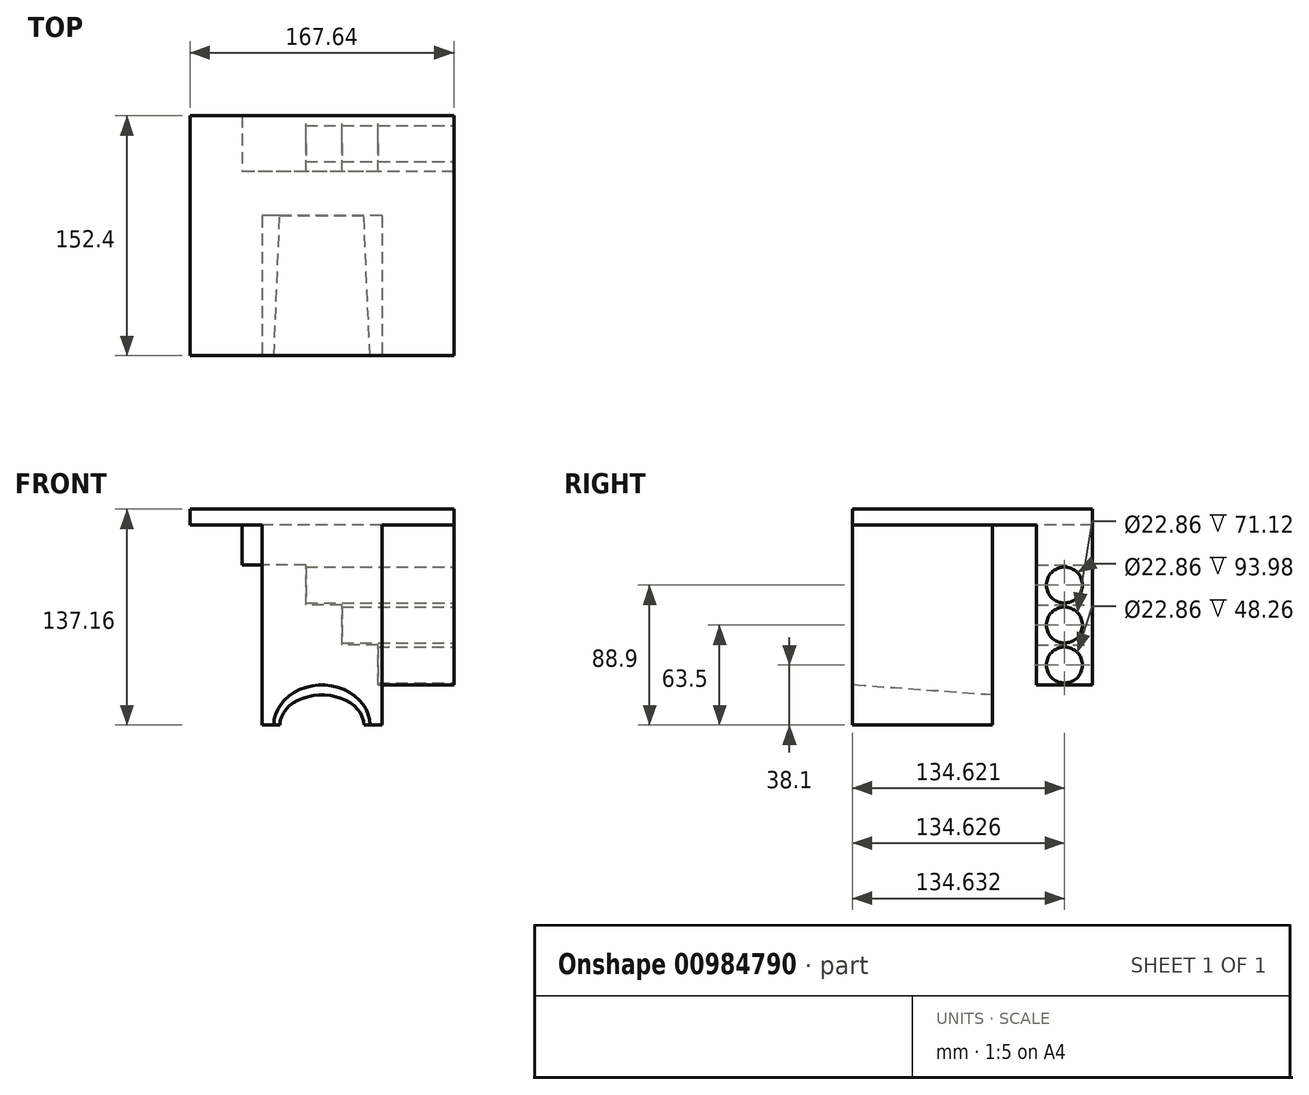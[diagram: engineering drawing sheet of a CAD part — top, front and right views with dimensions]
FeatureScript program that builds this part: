
annotation { "Feature Type Name" : "Feature", "Feature Type Description" : "" }
export const myFeature = defineFeature(function(context is Context, id is Id, definition is map)
    precondition{}
    {
        {
            var Q0;
            Q0=qCreatedBy(makeId("Top.planeOp"),FACE);
            var sketch = newSketch(context, id + "F0", { "sketchPlane" : qUnion([Q0])});
            skLineSegment(sketch, "E0.bottom", {"start": v(-69.25, 110.43) * mm, "end": v(32.35, 110.43) * mm});
            skLineSegment(sketch, "E0.top", {"start": v(-69.25, -41.97) * mm, "end": v(32.35, -41.97) * mm});
            skLineSegment(sketch, "E0.left", {"start": v(-69.25, 110.43) * mm, "end": v(-69.25, -41.97) * mm});
            skLineSegment(sketch, "E0.right", {"start": v(32.35, 110.43) * mm, "end": v(32.35, -41.97) * mm});
            skLineSegment(sketch, "E1", {"start": v(32.35, 110.43) * mm, "end": v(65.37, 110.43) * mm});
            skLineSegment(sketch, "E2", {"start": v(65.37, 110.43) * mm, "end": v(65.37, -41.97) * mm});
            skLineSegment(sketch, "E3", {"start": v(65.37, -41.97) * mm, "end": v(32.35, -41.97) * mm});
            skLineSegment(sketch, "E4.bottom", {"start": v(-69.25, 110.43) * mm, "end": v(-102.27, 110.43) * mm});
            skLineSegment(sketch, "E4.top", {"start": v(-69.25, -41.97) * mm, "end": v(-102.27, -41.97) * mm});
            skLineSegment(sketch, "E4.right", {"start": v(-102.27, 110.43) * mm, "end": v(-102.27, -41.97) * mm});
            skSolve(sketch);
        }
        {
            var Q0;
            Q0=makeQuery(id+"F0.imprint","IMPRINT",FACE,{"disambiguationData":[TD([[makeQuery(id+"F0.imprint","IMPRINT",EDGE,{"derivedFrom":sQuery(id+"F0.wireOp",EDGE,"E0.bottom")}),-1.0]])]});
            extrude(context, id + "F1", {"entities" : qUnion([Q0]), "depth" : 10.16 * mm, "offsetDistance" : 25.4 * mm});
        }
        {
            var Q0;
            Q0=makeQuery(id+"F1.opExtrude","CAP_FACE",FACE,{"disambiguationData":[OSD([sQuery(id+"F0.wireOp",EDGE,"E0.bottom"),sQuery(id+"F0.wireOp",EDGE,"E0.top"),sQuery(id+"F0.wireOp",EDGE,"E0.left"),sQuery(id+"F0.wireOp",EDGE,"E0.right")])],"isStart":true});
            var sketch = newSketch(context, id + "F2", { "sketchPlane" : qUnion([Q0])});
            skLineSegment(sketch, "E5", {"start": v(-18.45, -110.43) * mm, "end": v(-18.45, 53.26) * mm, "construction": true});
            skPoint(sketch, "E5.endSnap0", {"position": v(-18.45, 41.97) * mm});
            skLineSegment(sketch, "E6", {"start": v(32.35, -34.23) * mm, "end": v(-139.29, -34.23) * mm, "construction": true});
            skLineSegment(sketch, "E7.bottom", {"start": v(19.65, -46.93) * mm, "end": v(-56.55, -46.93) * mm});
            skLineSegment(sketch, "E7.top", {"start": v(19.65, 41.97) * mm, "end": v(-56.55, 41.97) * mm});
            skLineSegment(sketch, "E7.left", {"start": v(19.65, -46.93) * mm, "end": v(19.65, 41.97) * mm});
            skLineSegment(sketch, "E7.right", {"start": v(-56.55, -46.93) * mm, "end": v(-56.55, 41.97) * mm});
            skSolve(sketch);
        }
        {
            var Q0;
            Q0=makeQuery(id+"F2.imprint","IMPRINT",FACE,{"disambiguationData":[TD([[makeQuery(id+"F2.imprint","IMPRINT",EDGE,{"derivedFrom":sQuery(id+"F2.wireOp",EDGE,"E7.bottom")}),-1.0]])]});
            extrude(context, id + "F3", {"entities" : qUnion([Q0]), "operationType" : NewBodyOperationType.ADD, "depth" : 127 * mm, "offsetDistance" : 25.4 * mm});
        }
        {
            var Q0;
            Q0=makeQuery(id+"F3.boolean.opBoolean","MERGE",FACE,{"derivedFrom":[makeQuery(id+"F1.opExtrude","SWEPT_FACE",FACE,{"disambiguationData":[OSD([sQuery(id+"F0.wireOp",EDGE,"E0.top")])]}),makeQuery(id+"F3.opExtrude","SWEPT_FACE",FACE,{"disambiguationData":[OSD([sQuery(id+"F2.wireOp",EDGE,"E7.top")])]})]});
            var sketch = newSketch(context, id + "F4", { "sketchPlane" : qUnion([Q0])});
            skEllipse(sketch, "E8", {"center": v(-18.45, -127) * mm, "majorRadius": 30.48 * mm, "minorRadius": 25.4 * mm, "majorAxis": v(-1, 0)});
            skSolve(sketch);
        }
        {
            var Q0;
            Q0=makeQuery(id+"F3.opExtrude","SWEPT_FACE",FACE,{"disambiguationData":[OSD([sQuery(id+"F2.wireOp",EDGE,"E7.bottom")])]});
            var sketch = newSketch(context, id + "F5", { "sketchPlane" : qUnion([Q0])});
            skEllipse(sketch, "E9", {"center": v(18.45, -127) * mm, "majorRadius": 26.67 * mm, "minorRadius": 19.05 * mm, "majorAxis": v(-1, 0)});
            skSolve(sketch);
        }
        {
            var Q1;
            {var subQ0=sQuery(id+"F4.wireOp",EDGE,"E8");var subQ1=makeQuery(id+"F3.opExtrude","CAP_EDGE",EDGE,{"disambiguationData":[OSD([sQuery(id+"F2.wireOp",EDGE,"E7.top")])],"isStart":false});var subQ2=makeQuery(id+"F4.imprint","INTERSECT",VERTEX,{"disambiguationData":[OD(0.0)],"derivedFrom":[subQ1,subQ0]});Q1=makeQuery(id+"F4.imprint","IMPRINT",FACE,{"disambiguationData":[TD([[makeQuery(id+"F4.imprint","IMPRINT",EDGE,{"disambiguationData":[TD([[subQ2,1.0]])],"derivedFrom":subQ0}),1.0]])]});}
            var Q2;
            {var subQ0=sQuery(id+"F5.wireOp",EDGE,"E9");var subQ1=makeQuery(id+"F3.opExtrude","CAP_EDGE",EDGE,{"disambiguationData":[OSD([sQuery(id+"F2.wireOp",EDGE,"E7.bottom")])],"isStart":false});var subQ2=makeQuery(id+"F5.imprint","INTERSECT",VERTEX,{"disambiguationData":[OD(0.0)],"derivedFrom":[subQ1,subQ0]});Q2=makeQuery(id+"F5.imprint","IMPRINT",FACE,{"disambiguationData":[TD([[makeQuery(id+"F5.imprint","IMPRINT",EDGE,{"disambiguationData":[TD([[subQ2,1.0]])],"derivedFrom":subQ0}),1.0]])]});}
            loft(context, id + "F6", {"operationType" : NewBodyOperationType.REMOVE, "sheetProfilesArray" : [{ "sheetProfileEntities" : qUnion([Q1]) }, { "sheetProfileEntities" : qUnion([Q2]) }]});
        }
        {
            var Q0;
            Q0=makeQuery(id+"F0.imprint","IMPRINT",FACE,{"disambiguationData":[TD([[makeQuery(id+"F0.imprint","IMPRINT",EDGE,{"derivedFrom":sQuery(id+"F0.wireOp",EDGE,"E0.right")}),1.0]])]});
            extrude(context, id + "F7", {"entities" : qUnion([Q0]), "operationType" : NewBodyOperationType.ADD, "depth" : 10.16 * mm, "offsetDistance" : 25.4 * mm});
        }
        {
            var Q0;
            {var subQ0=sQuery(id+"F0.wireOp",EDGE,"E0.right");Q0=makeQuery(id+"F7.boolean.opBoolean","MERGE",FACE,{"derivedFrom":[makeQuery(id+"F1.opExtrude","CAP_FACE",FACE,{"disambiguationData":[OSD([sQuery(id+"F0.wireOp",EDGE,"E0.bottom"),sQuery(id+"F0.wireOp",EDGE,"E0.top"),sQuery(id+"F0.wireOp",EDGE,"E0.left"),subQ0])],"isStart":true}),makeQuery(id+"F7.opExtrude","CAP_FACE",FACE,{"disambiguationData":[OSD([subQ0,sQuery(id+"F0.wireOp",EDGE,"E1"),sQuery(id+"F0.wireOp",EDGE,"E2"),sQuery(id+"F0.wireOp",EDGE,"E3")])],"isStart":true})]});}
            var sketch = newSketch(context, id + "F8", { "sketchPlane" : qUnion([Q0])});
            skLineSegment(sketch, "E10.bottom", {"start": v(65.37, -110.43) * mm, "end": v(-102.27, -110.43) * mm});
            skLineSegment(sketch, "E10.top", {"start": v(65.37, -74.87) * mm, "end": v(-102.27, -74.87) * mm});
            skLineSegment(sketch, "E10.left", {"start": v(65.37, -110.43) * mm, "end": v(65.37, -74.87) * mm});
            skLineSegment(sketch, "E10.right", {"start": v(-102.27, -110.43) * mm, "end": v(-102.27, -74.87) * mm});
            skSolve(sketch);
        }
        {
            var Q0;
            Q0=makeQuery(id+"F8.imprint","IMPRINT",FACE,{"disambiguationData":[TD([[makeQuery(id+"F8.imprint","IMPRINT",EDGE,{"derivedFrom":sQuery(id+"F8.wireOp",EDGE,"E10.bottom")}),1.0]])]});
            extrude(context, id + "F9", {"entities" : qUnion([Q0]), "operationType" : NewBodyOperationType.ADD, "depth" : 101.6 * mm, "offsetDistance" : 25.4 * mm});
        }
        {
            var Q0;
            Q0=makeQuery(id+"F9.boolean.opBoolean","MERGE",FACE,{"derivedFrom":[makeQuery(id+"F7.boolean.opBoolean","MERGE",FACE,{"derivedFrom":[makeQuery(id+"F1.opExtrude","SWEPT_FACE",FACE,{"disambiguationData":[OSD([sQuery(id+"F0.wireOp",EDGE,"E0.bottom")])]}),makeQuery(id+"F7.opExtrude","SWEPT_FACE",FACE,{"disambiguationData":[OSD([sQuery(id+"F0.wireOp",EDGE,"E1")])]})]}),makeQuery(id+"F9.opExtrude","SWEPT_FACE",FACE,{"disambiguationData":[OSD([sQuery(id+"F8.wireOp",EDGE,"E10.bottom")])]})]});
            var sketch = newSketch(context, id + "F10", { "sketchPlane" : qUnion([Q0])});
            skLineSegment(sketch, "E11", {"start": v(-17.11, -101.6) * mm, "end": v(-17.11, -76.2) * mm});
            skLineSegment(sketch, "E12", {"start": v(-17.11, -76.2) * mm, "end": v(5.75, -76.2) * mm});
            skLineSegment(sketch, "E13", {"start": v(5.75, -76.2) * mm, "end": v(5.75, -50.8) * mm});
            skLineSegment(sketch, "E14", {"start": v(5.75, -50.8) * mm, "end": v(28.6, -50.8) * mm});
            skLineSegment(sketch, "E15", {"start": v(28.6, -50.8) * mm, "end": v(28.6, -25.4) * mm});
            skLineSegment(sketch, "E16", {"start": v(28.6, -25.4) * mm, "end": v(69.25, -25.4) * mm});
            skSolve(sketch);
        }
        {
            var Q0;
            {var subQ0=sQuery(id+"F10.wireOp",EDGE,"E11");Q0=makeQuery(id+"F10.imprint","IMPRINT",FACE,{"disambiguationData":[TD([[makeQuery(id+"F10.imprint","IMPRINT",EDGE,{"derivedFrom":subQ0}),-1.0]])]});}
            extrude(context, id + "F11", {"entities" : qUnion([Q0]), "operationType" : NewBodyOperationType.REMOVE, "oppositeDirection" : true, "depth" : 39.88 * mm, "offsetDistance" : 25.4 * mm});
        }
        {
            var Q0;
            Q0=makeQuery(id+"F9.boolean.opBoolean","MERGE",FACE,{"derivedFrom":[makeQuery(id+"F7.opExtrude","SWEPT_FACE",FACE,{"disambiguationData":[OSD([sQuery(id+"F0.wireOp",EDGE,"E2")])]}),makeQuery(id+"F9.opExtrude","SWEPT_FACE",FACE,{"disambiguationData":[OSD([sQuery(id+"F8.wireOp",EDGE,"E10.left")])]})]});
            var sketch = newSketch(context, id + "F12", { "sketchPlane" : qUnion([Q0])});
            skLineSegment(sketch, "E17", {"start": v(92.65, -101.6) * mm, "end": v(92.65, 10.16) * mm, "construction": true});
            skLineSegment(sketch, "E18", {"start": v(110.43, -76.2) * mm, "end": v(69.9, -76.2) * mm, "construction": true});
            skLineSegment(sketch, "E19", {"start": v(110.43, -50.8) * mm, "end": v(68.79, -50.8) * mm, "construction": true});
            skLineSegment(sketch, "E20", {"start": v(110.43, -25.4) * mm, "end": v(63.04, -25.4) * mm, "construction": true});
            skLineSegment(sketch, "E21", {"start": v(110.43, -88.9) * mm, "end": v(54.17, -88.9) * mm, "construction": true});
            skLineSegment(sketch, "E22", {"start": v(47.89, -63.5) * mm, "end": v(110.43, -63.5) * mm, "construction": true});
            skLineSegment(sketch, "E23", {"start": v(74.87, -38.1) * mm, "end": v(110.43, -38.1) * mm, "construction": true});
            skCircle(sketch, "E24", {"center": v(92.65, -88.9) * mm, "radius": 11.43 * mm});
            skCircle(sketch, "E25.0.1.0", {"center": v(92.66, -63.5) * mm, "radius": 11.43 * mm});
            skCircle(sketch, "E25.0.2.0", {"center": v(92.66, -38.1) * mm, "radius": 11.43 * mm});
            skLineSegment(sketch, "E25.direction1", {"start": v(92.65, -88.9) * mm, "end": v(116.02, -88.9) * mm, "construction": true});
            skLineSegment(sketch, "E25.direction2", {"start": v(92.65, -88.9) * mm, "end": v(92.66, -63.5) * mm, "construction": true});
            skSolve(sketch);
        }
        {
            var Q0;
            Q0=makeQuery(id+"F12.imprint","IMPRINT",FACE,{"disambiguationData":[TD([[makeQuery(id+"F12.imprint","IMPRINT",EDGE,{"derivedFrom":sQuery(id+"F12.wireOp",EDGE,"E24")}),1.0]])]});
            var Q1;
            Q1=makeQuery(id+"F12.imprint","IMPRINT",FACE,{"disambiguationData":[TD([[makeQuery(id+"F12.imprint","IMPRINT",EDGE,{"derivedFrom":sQuery(id+"F12.wireOp",EDGE,"E25.0.1.0")}),1.0]])]});
            var Q2;
            Q2=makeQuery(id+"F12.imprint","IMPRINT",FACE,{"disambiguationData":[TD([[makeQuery(id+"F12.imprint","IMPRINT",EDGE,{"derivedFrom":sQuery(id+"F12.wireOp",EDGE,"E25.0.2.0")}),1.0]])]});
            extrude(context, id + "F13", {"entities" : qUnion([Q0, Q1, Q2]), "operationType" : NewBodyOperationType.REMOVE, "oppositeDirection" : true, "depth" : 121.92 * mm, "offsetDistance" : 25.4 * mm});
        }
        {
            var Q0;
            Q0=makeQuery(id+"F0.imprint","IMPRINT",FACE,{"disambiguationData":[TD([[makeQuery(id+"F0.imprint","IMPRINT",EDGE,{"derivedFrom":sQuery(id+"F0.wireOp",EDGE,"E4.bottom")}),1.0]])]});
            extrude(context, id + "F14", {"entities" : qUnion([Q0]), "operationType" : NewBodyOperationType.ADD, "depth" : 10.16 * mm, "offsetDistance" : 25.4 * mm});
        }
    });
